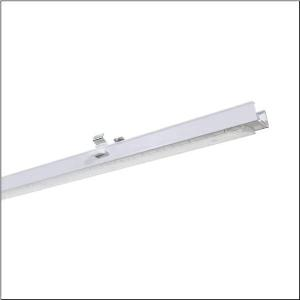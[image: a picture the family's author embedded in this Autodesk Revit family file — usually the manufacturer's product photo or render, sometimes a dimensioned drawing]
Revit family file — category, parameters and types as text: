
# Revit family: trunking_flex_31_51re18ma46b
name_source: partatom
category: Lighting Fixtures
units: mm (PartAtom-declared; Revit-internal decimal feet)

## family parameters
Cut with Voids When Loaded = No
Host = Face
Light Source = No
Part Type = Normal
Room Calculation Point = No
Round Connector Dimension = Use Diameter
Shared = No

## types (1)
- --- (1 x LED, 6400 lm, 40 W, 4000K)
    Apparent Load = 40 VA
    CIE Flux Codes = 71 89 97 97 100
    Color Rendering = 80
    Color Temperature = 4000K
    Default Elevation = 1800 mm
    Description = Trunking Flex 31, luminaire insert, of extruded aluminium section, coated, traffic white (RAL 9016), length: 1.172mm, width: 91mm, height: 53mm, LED rated luminous flux: 6.400lm, light colour: 840, control gear: ON/OFF Multilumen, with system connector: socket, mains connection: 220..240V, AC, 50/60Hz, rated input power: 40W, luminous flux adjustable on luminaire in four steps (3420/4540/5580/6630lm), connected load according to luminous flux setting (20/26/33/40W), primary light control with lens, of plastic, primary optical cover: cover, of PMMA, light emission: direct distribution, protection rating (complete): IP20, insulation class (complete): insulation class I (protective earthing), certification: CE, UKCA, impact resistance: IK02, permissible ambient temperature for indoor applications: -20..+40°C, packaging unit: 1 piece
    Height = 58 mm
    Lamp = 1 x LED
    Lamp Light Flux = 6400 lm
    Lamp Power = 40 W
    Lamp count = 1
    Length = 1172 mm
    Luminous efficacy = 160 lm/W
    Manufacturer = Siteco
    ModVariant = No
    Model = 51RE18MA46B
    Mounting Place = Ceiling
    Mounting Type = Pendant
    Number of Poles = 1
    OnlyDefault = Yes
    Power Factor = 1
    Product Name = Trunking Flex 31
    Product group = luminaire insert
    ProductGroupID = 901
    Protection Class = Protection class I
    Protection Degree = IP 20
    RLX_Detail_Level = 1
    RLX_Emergency_Light_Flux = 0 lm
    RLX_Emergency_Type = 0
    RLX_Emergency_Type_DB = No
    RlxData = <blob elided: 20033 chars, md5=bcaade74>
    Socket = socket
    Standby Power = 0 W
    System Light Flux = 6400 lm
    System Power = 40 W
    Type Comments = factory setting: luminous flux: 100 % | (ON | ON) | 300 mA
    Type Image = l_1266702.jpg
    URL = http://relux.com
    VarID = @adj_027059
    Voltage = 0 V
    Weight = 0.00 kg
    Width = 65 mm

## geometry (parser evidence)
native form markers: Blend x4, Sweep x11
no freeform markers — native parametric forms only
